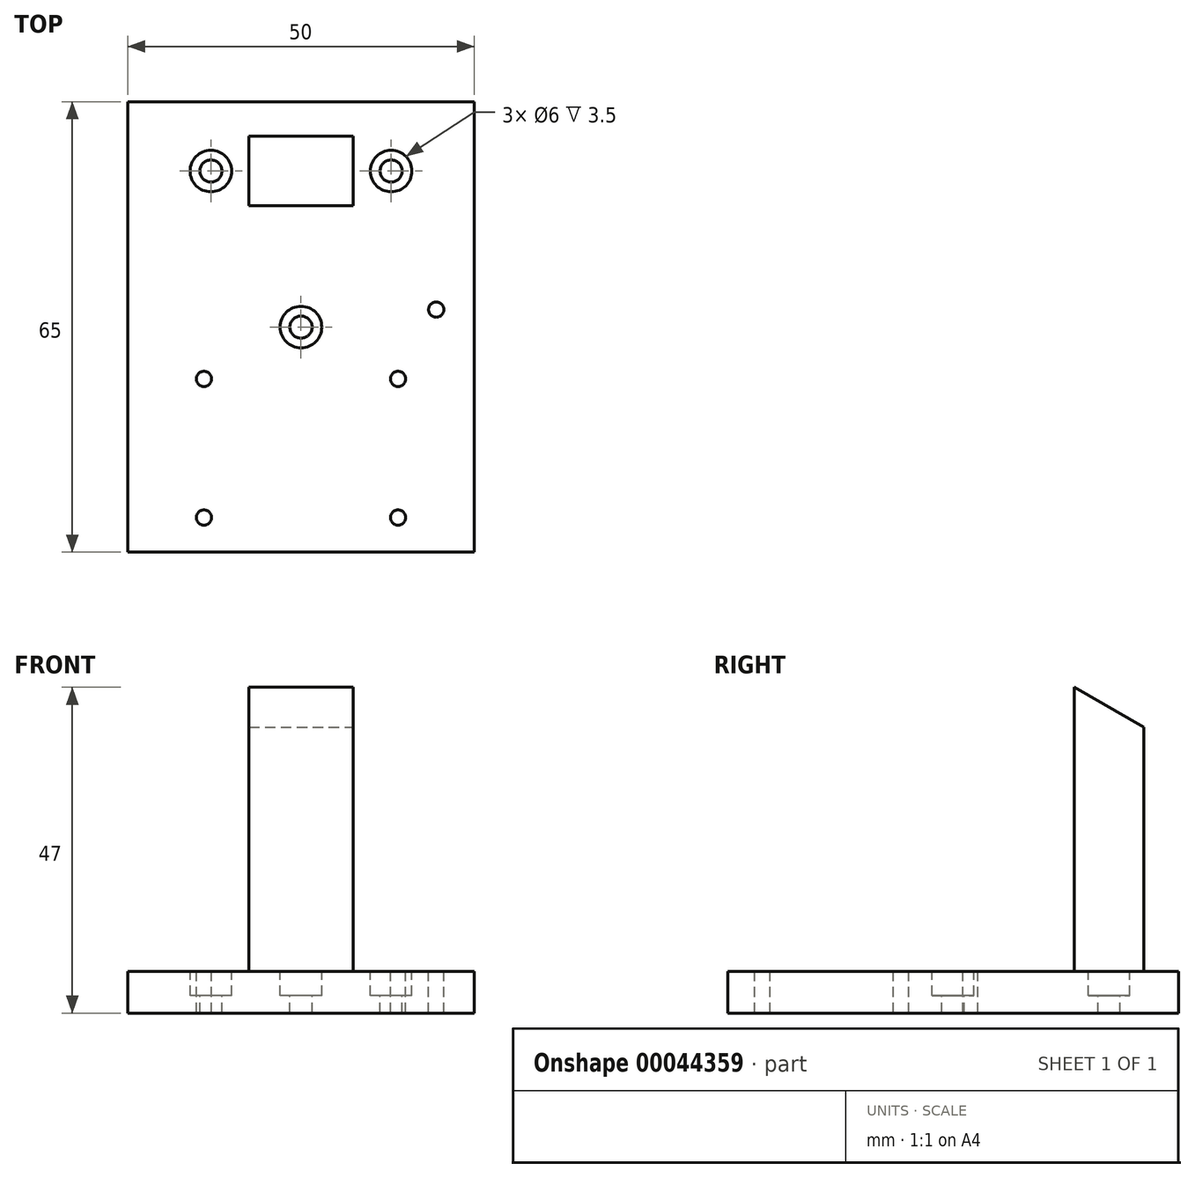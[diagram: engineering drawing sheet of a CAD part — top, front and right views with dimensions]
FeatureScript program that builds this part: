
annotation { "Feature Type Name" : "Feature", "Feature Type Description" : "" }
export const myFeature = defineFeature(function(context is Context, id is Id, definition is map)
    precondition{}
    {
        {
            var Q0;
            Q0=qCreatedBy(makeId("Top.planeOp"),FACE);
            var sketch = newSketch(context, id + "F0", { "sketchPlane" : qUnion([Q0])});
            skLineSegment(sketch, "E0.bottom", {"start": v(0, 0) * mm, "end": v(50, 0) * mm});
            skLineSegment(sketch, "E0.top", {"start": v(0, 65) * mm, "end": v(50, 65) * mm});
            skLineSegment(sketch, "E0.left", {"start": v(0, 0) * mm, "end": v(0, 65) * mm});
            skLineSegment(sketch, "E0.right", {"start": v(50, 0) * mm, "end": v(50, 65) * mm});
            skSolve(sketch);
        }
        {
            var Q0;
            Q0=qSketchRegion(id+"F0",true);
            extrude(context, id + "F1", {"entities" : qUnion([Q0]), "depth" : 6 * mm});
        }
        {
            var Q0;
            Q0=makeQuery(id+"F1.opExtrude","CAP_FACE",FACE,{"disambiguationData":[OSD([sQuery(id+"F0.wireOp",EDGE,"E0.bottom"),sQuery(id+"F0.wireOp",EDGE,"E0.top"),sQuery(id+"F0.wireOp",EDGE,"E0.left"),sQuery(id+"F0.wireOp",EDGE,"E0.right")])],"isStart":false});
            var sketch = newSketch(context, id + "F2", { "sketchPlane" : qUnion([Q0])});
            skLineSegment(sketch, "E1.bottom", {"start": v(17.5, 60) * mm, "end": v(32.5, 60) * mm});
            skLineSegment(sketch, "E1.top", {"start": v(17.5, 50) * mm, "end": v(32.5, 50) * mm});
            skLineSegment(sketch, "E1.left", {"start": v(17.5, 60) * mm, "end": v(17.5, 50) * mm});
            skLineSegment(sketch, "E1.right", {"start": v(32.5, 60) * mm, "end": v(32.5, 50) * mm});
            skLineSegment(sketch, "E2", {"start": v(32.5, 60) * mm, "end": v(50, 60) * mm});
            skLineSegment(sketch, "E3", {"start": v(17.5, 60) * mm, "end": v(0, 60) * mm});
            skSolve(sketch);
        }
        {
            var Q0;
            Q0=qSketchRegion(id+"F2",true);
            extrude(context, id + "F3", {"entities" : qUnion([Q0]), "operationType" : NewBodyOperationType.ADD, "depth" : 41 * mm});
        }
        {
            var Q0;
            Q0=makeQuery(id+"F1.opExtrude","CAP_FACE",FACE,{"disambiguationData":[OSD([sQuery(id+"F0.wireOp",EDGE,"E0.bottom"),sQuery(id+"F0.wireOp",EDGE,"E0.top"),sQuery(id+"F0.wireOp",EDGE,"E0.left"),sQuery(id+"F0.wireOp",EDGE,"E0.right")])],"isStart":false});
            var sketch = newSketch(context, id + "F4", { "sketchPlane" : qUnion([Q0])});
            skPoint(sketch, "E4", {"position": v(12, 55) * mm});
            skPoint(sketch, "E5", {"position": v(38, 55) * mm});
            skLineSegment(sketch, "E6", {"start": v(12, 55) * mm, "end": v(38, 55) * mm});
            skLineSegment(sketch, "E7", {"start": v(38, 55) * mm, "end": v(50, 55) * mm});
            skLineSegment(sketch, "E8", {"start": v(12, 55) * mm, "end": v(0, 55) * mm});
            skPoint(sketch, "E9", {"position": v(25, 32.48) * mm});
            skSolve(sketch);
        }
        {
            var Q0;
            Q0=sQuery(id+"F4.wireOp",VERTEX,"E4");
            var Q1;
            Q1=sQuery(id+"F4.wireOp",VERTEX,"E5");
            var Q2;
            Q2=sQuery(id+"F4.wireOp",VERTEX,"E9");
            var Q3;
            Q3=makeQuery(id+"F1.opExtrude","SWEPT_BODY",BODY,{"disambiguationData":[OSD([sQuery(id+"F0.wireOp",EDGE,"E0.bottom"),sQuery(id+"F0.wireOp",EDGE,"E0.top"),sQuery(id+"F0.wireOp",EDGE,"E0.left"),sQuery(id+"F0.wireOp",EDGE,"E0.right")])]});
            hole(context, id + "F5", {"style" : HoleStyle.C_BORE, "holeDiameter" : 3.2 * mm, "cBoreDiameter" : 6 * mm, "cBoreDepth" : 3.5 * mm, "endStyle" : HoleEndStyle.THROUGH, "locations" : qUnion([Q0, Q1, Q2]), "scope" : qUnion([Q3])});
        }
        {
            var Q0;
            Q0=makeQuery(id+"F1.opExtrude","CAP_FACE",FACE,{"disambiguationData":[OSD([sQuery(id+"F0.wireOp",EDGE,"E0.bottom"),sQuery(id+"F0.wireOp",EDGE,"E0.top"),sQuery(id+"F0.wireOp",EDGE,"E0.left"),sQuery(id+"F0.wireOp",EDGE,"E0.right")])],"isStart":false});
            var sketch = newSketch(context, id + "F6", { "sketchPlane" : qUnion([Q0])});
            skLineSegment(sketch, "E10.bottom", {"start": v(11, 25) * mm, "end": v(39, 25) * mm});
            skLineSegment(sketch, "E10.top", {"start": v(11, 5) * mm, "end": v(39, 5) * mm});
            skLineSegment(sketch, "E10.left", {"start": v(11, 25) * mm, "end": v(11, 5) * mm});
            skLineSegment(sketch, "E10.right", {"start": v(39, 25) * mm, "end": v(39, 5) * mm});
            skLineSegment(sketch, "E11", {"start": v(39, 25) * mm, "end": v(50, 25) * mm});
            skLineSegment(sketch, "E12", {"start": v(11, 25) * mm, "end": v(0, 25) * mm});
            skPoint(sketch, "E13", {"position": v(44.5, 35) * mm});
            skPoint(sketch, "E13.positionSnap0", {"position": v(44.5, 25) * mm});
            skSolve(sketch);
        }
        {
            var Q0;
            Q0=sQuery(id+"F6.wireOp",VERTEX,"E12.start");
            var Q1;
            Q1=sQuery(id+"F6.wireOp",VERTEX,"E11.start");
            var Q2;
            Q2=sQuery(id+"F6.wireOp",VERTEX,"E10.right.end");
            var Q3;
            Q3=sQuery(id+"F6.wireOp",VERTEX,"E10.top.start");
            var Q4;
            Q4=sQuery(id+"F6.wireOp",VERTEX,"E13");
            var Q5;
            Q5=makeQuery(id+"F1.opExtrude","SWEPT_BODY",BODY,{"disambiguationData":[OSD([sQuery(id+"F0.wireOp",EDGE,"E0.bottom"),sQuery(id+"F0.wireOp",EDGE,"E0.top"),sQuery(id+"F0.wireOp",EDGE,"E0.left"),sQuery(id+"F0.wireOp",EDGE,"E0.right")])]});
            hole(context, id + "F7", {"style" : HoleStyle.SIMPLE, "holeDiameter" : 2.2 * mm, "endStyle" : HoleEndStyle.THROUGH, "locations" : qUnion([Q0, Q1, Q2, Q3, Q4]), "scope" : qUnion([Q5])});
        }
        {
            var Q0;
            Q0=makeQuery(id+"F3.opExtrude","SWEPT_FACE",FACE,{"disambiguationData":[OSD([sQuery(id+"F2.wireOp",EDGE,"E1.right")])]});
            var sketch = newSketch(context, id + "F8", { "sketchPlane" : qUnion([Q0])});
            skLineSegment(sketch, "E14", {"start": v(50, 47) * mm, "end": v(60, 41.23) * mm});
            skLineSegment(sketch, "E15", {"start": v(60, 41.23) * mm, "end": v(60, 47) * mm});
            skLineSegment(sketch, "E16", {"start": v(60, 47) * mm, "end": v(50, 47) * mm});
            skSolve(sketch);
        }
        {
            var Q0;
            Q0 = qSketchRegion(id + "F8", true);
            var Q1;
            Q1=makeQuery(id+"F3.opExtrude","SWEPT_FACE",FACE,{"disambiguationData":[OSD([sQuery(id+"F2.wireOp",EDGE,"E1.left")])]});
            extrude(context, id + "F9", {"entities" : qUnion([Q0]), "operationType" : NewBodyOperationType.REMOVE, "endBound" : BoundingType.UP_TO_SURFACE, "oppositeDirection" : true, "endBoundEntityFace" : qUnion([Q1]), "depth" : 25 * mm});
        }
    });
